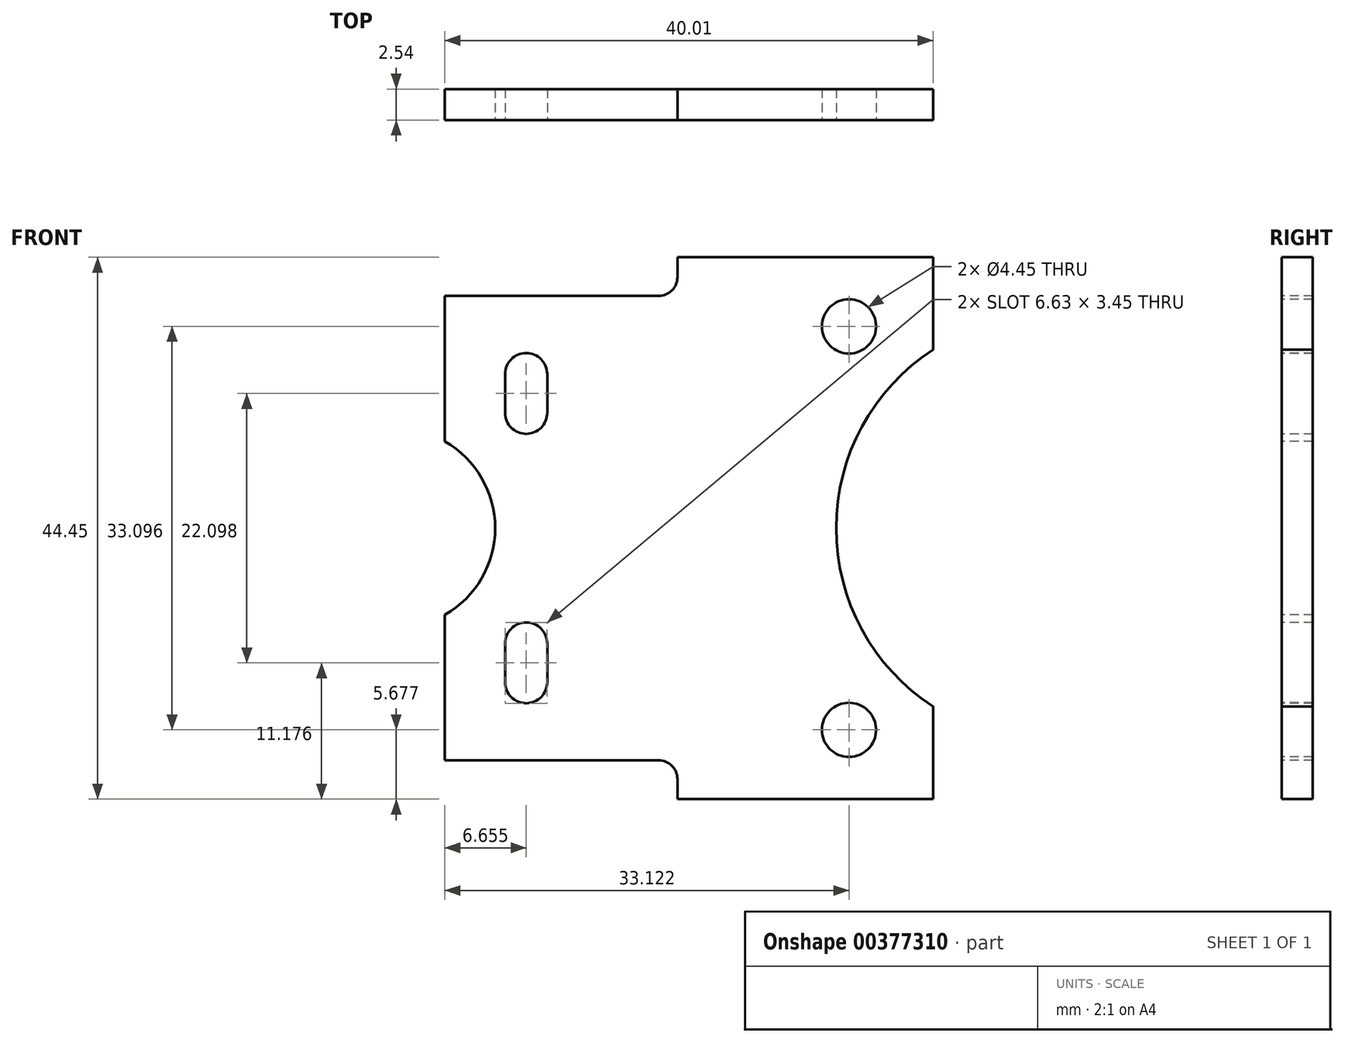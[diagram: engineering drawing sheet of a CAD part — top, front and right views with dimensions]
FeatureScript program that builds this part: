
annotation { "Feature Type Name" : "Feature", "Feature Type Description" : "" }
export const myFeature = defineFeature(function(context is Context, id is Id, definition is map)
    precondition{}
    {
        {
            var Q0;
            Q0=qCreatedBy(makeId("Top.planeOp"),FACE);
            var sketch = newSketch(context, id + "F0", { "sketchPlane" : qUnion([Q0])});
            skLineSegment(sketch, "E0.bottom", {"start": v(0, 0) * mm, "end": v(-30.48, 0) * mm});
            skLineSegment(sketch, "E0.top", {"start": v(0, 2.54) * mm, "end": v(-30.48, 2.54) * mm});
            skLineSegment(sketch, "E0.left", {"start": v(0, 0) * mm, "end": v(0, 2.54) * mm});
            skLineSegment(sketch, "E0.right", {"start": v(-30.48, 0) * mm, "end": v(-30.48, 2.54) * mm});
            skLineSegment(sketch, "E1", {"start": v(0, 2.54) * mm, "end": v(9.52, 2.54) * mm});
            skLineSegment(sketch, "E2", {"start": v(9.52, 2.54) * mm, "end": v(9.53, 0) * mm});
            skLineSegment(sketch, "E3", {"start": v(9.52, 0) * mm, "end": v(0, 0) * mm});
            skSolve(sketch);
        }
        {
            var Q0;
            Q0=makeQuery(id+"F0.imprint","IMPRINT",FACE,{"disambiguationData":[TD([[makeQuery(id+"F0.imprint","IMPRINT",EDGE,{"derivedFrom":sQuery(id+"F0.wireOp",EDGE,"E0.bottom")}),-1.0]])]});
            extrude(context, id + "F1", {"entities" : qUnion([Q0]), "depth" : 44.45 * mm});
        }
        {
            var Q0;
            Q0=makeQuery(id+"F1.opExtrude","SWEPT_FACE",FACE,{"disambiguationData":[OSD([sQuery(id+"F0.wireOp",EDGE,"E0.bottom")])]});
            var sketch = newSketch(context, id + "F2", { "sketchPlane" : qUnion([Q0])});
            skLineSegment(sketch, "E4", {"start": v(-30.48, 22.23) * mm, "end": v(-26.37, 22.23) * mm, "construction": true});
            skPoint(sketch, "E5", {"position": v(-30.48, 29.34) * mm});
            skPoint(sketch, "E6", {"position": v(-30.48, 15.11) * mm});
            skArc(sketch, "E7", {"start": v(-30.48, 15.11) * mm, "mid": v(-26.37, 22.23) * mm, "end": v(-30.48, 29.34) * mm});
            skLineSegment(sketch, "E8", {"start": v(-26.37, 22.23) * mm, "end": v(-23.83, 22.23) * mm, "construction": true});
            skLineSegment(sketch, "E9", {"start": v(-23.83, 33.27) * mm, "end": v(-23.83, 12.76) * mm, "construction": true});
            skLineSegment(sketch, "E10", {"start": v(-23.83, 33.27) * mm, "end": v(-23.83, 34.86) * mm, "construction": true});
            skLineSegment(sketch, "E11", {"start": v(-23.83, 11.18) * mm, "end": v(-23.83, 9.59) * mm, "construction": true});
            skLineSegment(sketch, "E12", {"start": v(-23.83, 33.27) * mm, "end": v(-23.83, 31.69) * mm, "construction": true});
            skArc(sketch, "E13", {"start": v(-22.1, 34.86) * mm, "mid": v(-23.83, 36.59) * mm, "end": v(-25.55, 34.86) * mm});
            skArc(sketch, "E14", {"start": v(-25.55, 31.69) * mm, "mid": v(-23.83, 29.96) * mm, "end": v(-22.1, 31.69) * mm});
            skArc(sketch, "E15", {"start": v(-22.1, 12.76) * mm, "mid": v(-23.83, 14.5) * mm, "end": v(-25.55, 12.76) * mm});
            skArc(sketch, "E16", {"start": v(-25.55, 9.59) * mm, "mid": v(-23.83, 7.86) * mm, "end": v(-22.1, 9.59) * mm});
            skLineSegment(sketch, "E17", {"start": v(-25.55, 12.76) * mm, "end": v(-25.55, 9.59) * mm});
            skLineSegment(sketch, "E18", {"start": v(-22.1, 12.76) * mm, "end": v(-22.1, 9.59) * mm});
            skLineSegment(sketch, "E19", {"start": v(-25.55, 34.86) * mm, "end": v(-25.55, 31.69) * mm});
            skLineSegment(sketch, "E20", {"start": v(-22.1, 34.86) * mm, "end": v(-22.1, 31.69) * mm});
            skLineSegment(sketch, "E21.trimOffspring", {"start": v(-23.83, 11.18) * mm, "end": v(-23.83, 12.76) * mm, "construction": true});
            skLineSegment(sketch, "E22.bottom", {"start": v(-30.48, 3.17) * mm, "end": v(-11.43, 3.17) * mm});
            skLineSegment(sketch, "E22.top", {"start": v(-30.48, 0) * mm, "end": v(-11.43, 0) * mm});
            skLineSegment(sketch, "E22.left", {"start": v(-30.48, 3.17) * mm, "end": v(-30.48, 0) * mm});
            skLineSegment(sketch, "E22.right", {"start": v(-11.43, 3.17) * mm, "end": v(-11.43, 0) * mm});
            skLineSegment(sketch, "E23.bottom", {"start": v(-30.48, 44.45) * mm, "end": v(-11.43, 44.45) * mm});
            skLineSegment(sketch, "E23.top", {"start": v(-30.48, 41.28) * mm, "end": v(-11.43, 41.28) * mm});
            skLineSegment(sketch, "E23.left", {"start": v(-30.48, 44.45) * mm, "end": v(-30.48, 41.28) * mm});
            skLineSegment(sketch, "E23.right", {"start": v(-11.43, 44.45) * mm, "end": v(-11.43, 41.28) * mm});
            skLineSegment(sketch, "E24", {"start": v(-11.43, 41.28) * mm, "end": v(-11.43, 3.17) * mm, "construction": true});
            skSolve(sketch);
        }
        {
            var Q0;
            Q0=makeQuery(id+"F0.imprint","IMPRINT",FACE,{"disambiguationData":[TD([[makeQuery(id+"F0.imprint","IMPRINT",EDGE,{"derivedFrom":sQuery(id+"F0.wireOp",EDGE,"E0.left")}),-1.0]])]});
            extrude(context, id + "F3", {"entities" : qUnion([Q0]), "operationType" : NewBodyOperationType.ADD, "depth" : 44.45 * mm});
        }
        {
            var Q0;
            Q0=makeQuery(id+"F3.boolean.opBoolean","MERGE",FACE,{"derivedFrom":[makeQuery(id+"F1.opExtrude","SWEPT_FACE",FACE,{"disambiguationData":[OSD([sQuery(id+"F0.wireOp",EDGE,"E0.bottom")])]}),makeQuery(id+"F3.opExtrude","SWEPT_FACE",FACE,{"disambiguationData":[OSD([sQuery(id+"F0.wireOp",EDGE,"E3")])]})]});
            var sketch = newSketch(context, id + "F4", { "sketchPlane" : qUnion([Q0])});
            skCircle(sketch, "E25", {"center": v(2.64, 38.77) * mm, "radius": 2.22 * mm});
            skCircle(sketch, "E26", {"center": v(2.64, 5.68) * mm, "radius": 2.22 * mm});
            skPoint(sketch, "E27", {"position": v(9.53, 5.68) * mm});
            skPoint(sketch, "E28", {"position": v(9.53, 38.77) * mm});
            skPoint(sketch, "E29", {"position": v(0, 22.23) * mm});
            skLineSegment(sketch, "E30", {"start": v(0, 0) * mm, "end": v(0, 44.45) * mm, "construction": true});
            skLineSegment(sketch, "E31", {"start": v(0, 22.23) * mm, "end": v(19.05, 22.23) * mm, "construction": true});
            skArc(sketch, "E32", {"start": v(9.52, 36.86) * mm, "mid": v(1.59, 22.23) * mm, "end": v(9.53, 7.59) * mm});
            skPoint(sketch, "E33", {"position": v(9.52, 36.86) * mm});
            skPoint(sketch, "E34", {"position": v(9.53, 7.59) * mm});
            skSolve(sketch);
        }
        {
            var Q0;
            {var subQ0=sQuery(id+"F4.wireOp",EDGE,"oErodHu0-SVqe-cXD9-A2Iy-klHVv3QFz86o");Q0=makeQuery(id+"F4.imprint","IMPRINT",FACE,{"disambiguationData":[TD([[makeQuery(id+"F4.imprint","IMPRINT",EDGE,{"derivedFrom":subQ0}),1.0]])]});}
            var Q1;
            Q1=makeQuery(id+"F4.imprint","IMPRINT",FACE,{"disambiguationData":[TD([[makeQuery(id+"F4.imprint","IMPRINT",EDGE,{"derivedFrom":sQuery(id+"F4.wireOp",EDGE,"E25")}),1.0]])]});
            var Q2;
            Q2=makeQuery(id+"F4.imprint","IMPRINT",FACE,{"disambiguationData":[TD([[makeQuery(id+"F4.imprint","IMPRINT",EDGE,{"derivedFrom":sQuery(id+"F4.wireOp",EDGE,"E26")}),1.0]])]});
            var Q3;
            Q3=makeQuery(id+"F2.imprint","IMPRINT",FACE,{"disambiguationData":[TD([[makeQuery(id+"F2.imprint","IMPRINT",EDGE,{"derivedFrom":sQuery(id+"F2.wireOp",EDGE,"E15")}),1.0]])]});
            var Q4;
            Q4=makeQuery(id+"F2.imprint","IMPRINT",FACE,{"disambiguationData":[TD([[makeQuery(id+"F2.imprint","IMPRINT",EDGE,{"derivedFrom":sQuery(id+"F2.wireOp",EDGE,"E13")}),1.0]])]});
            var Q5;
            {var subQ0=sQuery(id+"F2.wireOp",EDGE,"E7");Q5=makeQuery(id+"F2.imprint","IMPRINT",FACE,{"disambiguationData":[TD([[makeQuery(id+"F2.imprint","IMPRINT",EDGE,{"derivedFrom":subQ0}),1.0]])]});}
            var Q6;
            {var subQ0=sQuery(id+"F4.wireOp",EDGE,"E32");Q6=makeQuery(id+"F4.imprint","IMPRINT",FACE,{"disambiguationData":[TD([[makeQuery(id+"F4.imprint","IMPRINT",EDGE,{"derivedFrom":subQ0}),1.0]])]});}
            extrude(context, id + "F5", {"entities" : qUnion([Q0, Q1, Q2, Q3, Q4, Q5, Q6]), "operationType" : NewBodyOperationType.REMOVE, "oppositeDirection" : true, "depth" : 25.4 * mm});
        }
        {
            var Q0;
            Q0=makeQuery(id+"F2.imprint","IMPRINT",FACE,{"disambiguationData":[TD([[makeQuery(id+"F2.imprint","IMPRINT",EDGE,{"derivedFrom":sQuery(id+"F2.wireOp",EDGE,"E23.bottom")}),1.0]])]});
            var Q1;
            Q1=makeQuery(id+"F2.imprint","IMPRINT",FACE,{"disambiguationData":[TD([[makeQuery(id+"F2.imprint","IMPRINT",EDGE,{"derivedFrom":sQuery(id+"F2.wireOp",EDGE,"E22.bottom")}),-1.0]])]});
            extrude(context, id + "F6", {"entities" : qUnion([Q0, Q1]), "operationType" : NewBodyOperationType.REMOVE, "oppositeDirection" : true, "depth" : 25.4 * mm});
        }
        {
            var Q0;
            Q0=makeQuery(id+"F6.boolean.opBoolean","COPY",EDGE,{"derivedFrom":makeQuery(id+"F6.opExtrude","SWEPT_EDGE",EDGE,{"disambiguationData":[OSD([sQuery(id+"F2.wireOp",EDGE,"E23.top"),sQuery(id+"F2.wireOp",EDGE,"E23.right")])]})});
            var Q1;
            Q1=makeQuery(id+"F6.boolean.opBoolean","COPY",EDGE,{"derivedFrom":makeQuery(id+"F6.opExtrude","SWEPT_EDGE",EDGE,{"disambiguationData":[OSD([sQuery(id+"F0.wireOp",EDGE,"E0.bottom"),sQuery(id+"F2.wireOp",EDGE,"E23.bottom"),sQuery(id+"F2.wireOp",EDGE,"E23.right")])]})});
            var Q2;
            Q2=makeQuery(id+"F6.boolean.opBoolean","COPY",EDGE,{"derivedFrom":makeQuery(id+"F6.opExtrude","SWEPT_EDGE",EDGE,{"disambiguationData":[OSD([sQuery(id+"F0.wireOp",EDGE,"E0.bottom"),sQuery(id+"F2.wireOp",EDGE,"E22.top"),sQuery(id+"F2.wireOp",EDGE,"E22.right")])]})});
            var Q3;
            Q3=makeQuery(id+"F6.boolean.opBoolean","COPY",EDGE,{"derivedFrom":makeQuery(id+"F6.opExtrude","SWEPT_EDGE",EDGE,{"disambiguationData":[OSD([sQuery(id+"F2.wireOp",EDGE,"E22.bottom"),sQuery(id+"F2.wireOp",EDGE,"E22.right")])]})});
            fillet(context, id + "F7", {"entities" : qUnion([Q0, Q1, Q2, Q3]), "radius" : 1.52 * mm, "tangentPropagation" : true, "allowEdgeOverflow" : false});
        }
    });
